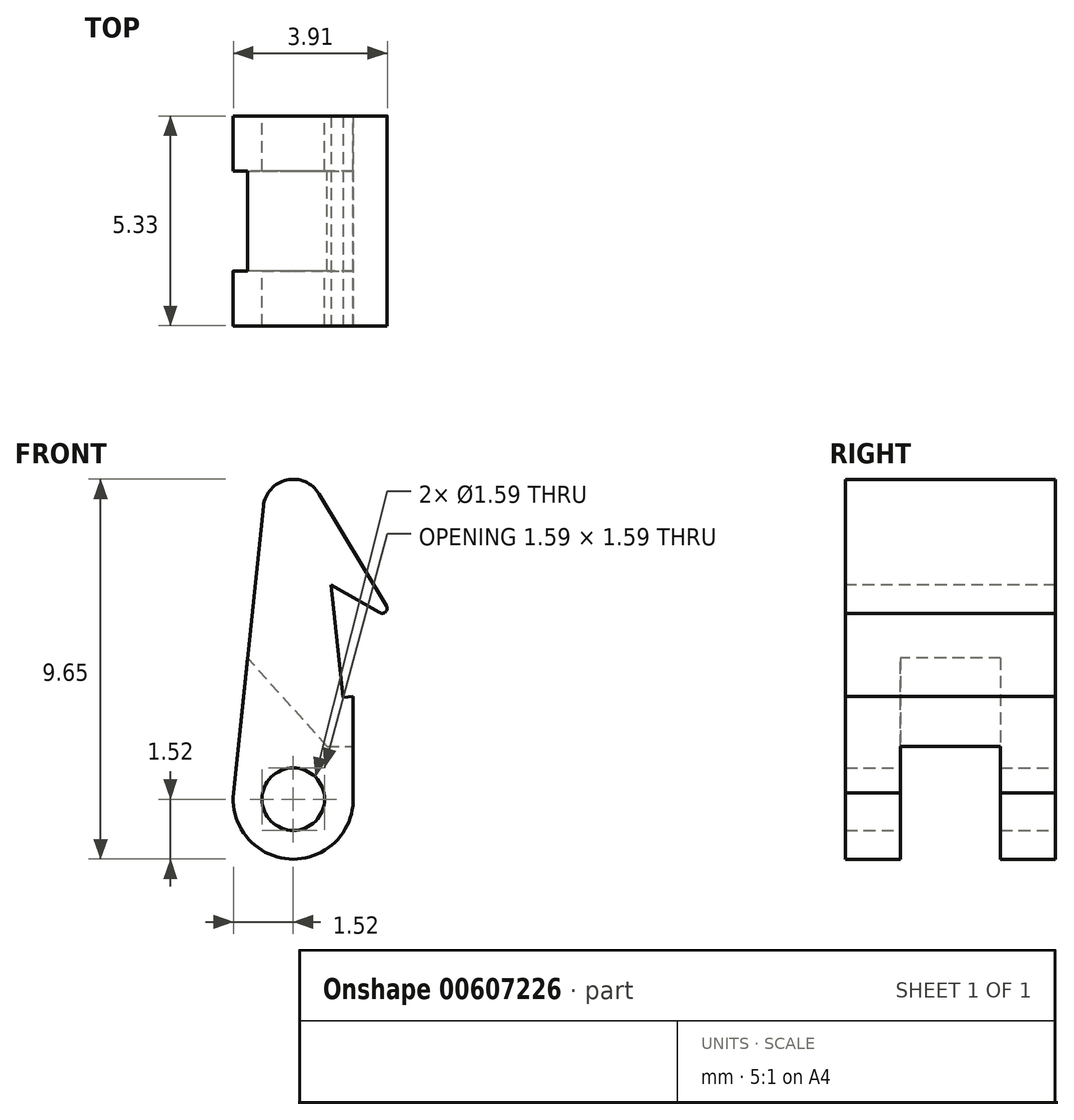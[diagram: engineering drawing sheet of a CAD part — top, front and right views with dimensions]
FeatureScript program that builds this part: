
annotation { "Feature Type Name" : "Feature", "Feature Type Description" : "" }
export const myFeature = defineFeature(function(context is Context, id is Id, definition is map)
    precondition{}
    {
        {
            var Q0;
            Q0=qCreatedBy(makeId("Front.planeOp"),FACE);
            var sketch = newSketch(context, id + "F0", { "sketchPlane" : qUnion([Q0])});
            skArc(sketch, "E0", {"start": v(1.52, 0.16) * mm, "mid": v(0, -1.52) * mm, "end": v(-1.52, 0.16) * mm});
            skLineSegment(sketch, "E1", {"start": v(-1.52, 0.16) * mm, "end": v(-0.76, 7.44) * mm});
            skArc(sketch, "E2", {"start": v(-0.76, 7.44) * mm, "mid": v(0, 8.13) * mm, "end": v(0.76, 7.44) * mm});
            skLineSegment(sketch, "E3", {"start": v(0.76, 7.44) * mm, "end": v(1.52, 0.16) * mm});
            skCircle(sketch, "E4", {"center": v(0, 0) * mm, "radius": 0.8 * mm});
            skSolve(sketch);
        }
        {
            var Q0;
            Q0 = qSketchRegion(id + "F0", true);
            extrude(context, id + "F1", {"entities" : qUnion([Q0]), "depth" : 5.33 * mm, "offsetDistance" : 25.4 * mm});
        }
        {
            var Q0;
            Q0=makeQuery(id+"F1.opExtrude","CAP_FACE",FACE,{"disambiguationData":[OSD([sQuery(id+"F0.wireOp",EDGE,"E0"),sQuery(id+"F0.wireOp",EDGE,"E1"),sQuery(id+"F0.wireOp",EDGE,"E2"),sQuery(id+"F0.wireOp",EDGE,"E3")])],"isStart":false});
            var sketch = newSketch(context, id + "F2", { "sketchPlane" : qUnion([Q0])});
            skLineSegment(sketch, "E5", {"start": v(0.65, 7.76) * mm, "end": v(2.62, 4.5) * mm});
            skLineSegment(sketch, "E6", {"start": v(2.62, 4.5) * mm, "end": v(0.97, 5.44) * mm});
            skLineSegment(sketch, "E7.0", {"start": v(0.76, 7.44) * mm, "end": v(1.52, 0.16) * mm});
            skArc(sketch, "E8.0", {"start": v(-0.76, 7.44) * mm, "mid": v(0, 8.13) * mm, "end": v(0.76, 7.44) * mm});
            skLineSegment(sketch, "E9", {"start": v(1.52, 0.16) * mm, "end": v(1.52, 2.61) * mm});
            skLineSegment(sketch, "E10", {"start": v(1.52, 2.61) * mm, "end": v(1.26, 2.59) * mm});
            skSolve(sketch);
        }
        {
            var Q0;
            Q0 = qSketchRegion(id + "F2", true);
            var Q1;
            {var subQ0=sQuery(id+"F2.wireOp",EDGE,"E5");Q1=makeQuery(id+"F2.imprint","IMPRINT",FACE,{"disambiguationData":[TD([[makeQuery(id+"F2.imprint","IMPRINT",EDGE,{"derivedFrom":subQ0}),-1.0]])]});}
            var Q2;
            Q2=makeQuery(id+"F1.opExtrude","CAP_FACE",FACE,{"disambiguationData":[OSD([sQuery(id+"F0.wireOp",EDGE,"E0"),sQuery(id+"F0.wireOp",EDGE,"E1"),sQuery(id+"F0.wireOp",EDGE,"E2"),sQuery(id+"F0.wireOp",EDGE,"E3"),sQuery(id+"F0.wireOp",EDGE,"E4")])],"isStart":true});
            extrude(context, id + "F3", {"entities" : qUnion([Q0, Q1]), "operationType" : NewBodyOperationType.ADD, "endBound" : BoundingType.UP_TO_SURFACE, "oppositeDirection" : true, "depth" : 25.4 * mm, "endBoundEntityFace" : qUnion([Q2]), "offsetDistance" : 25.4 * mm});
        }
        {
            var Q0;
            Q0=makeQuery(id+"F3.opExtrude","SWEPT_EDGE",EDGE,{"disambiguationData":[OSD([sQuery(id+"F2.wireOp",EDGE,"E5"),sQuery(id+"F2.wireOp",EDGE,"E6")])]});
            var Q1;
            Q1=makeQuery(id+"F3.opExtrude","SWEPT_EDGE",EDGE,{"disambiguationData":[OSD([sQuery(id+"F2.wireOp",EDGE,"E6"),sQuery(id+"F2.wireOp",EDGE,"E7.0")])]});
            fillet(context, id + "F4", {"entities" : qUnion([Q0, Q1]), "radius" : 0.13 * mm, "tangentPropagation" : true, "allowEdgeOverflow" : false});
        }
        {
            var Q0;
            Q0=makeQuery(id+"F3.opExtrude","SWEPT_FACE",FACE,{"disambiguationData":[OSD([sQuery(id+"F2.wireOp",EDGE,"E9")])]});
            var sketch = newSketch(context, id + "F5", { "sketchPlane" : qUnion([Q0])});
            skLineSegment(sketch, "E11.0.0", {"start": v(0, 0.16) * mm, "end": v(0, -1.52) * mm, "construction": true});
            skLineSegment(sketch, "E11.0.2", {"start": v(-5.33, 0.16) * mm, "end": v(-5.33, -1.52) * mm, "construction": true});
            skLineSegment(sketch, "E12.bottom", {"start": v(-3.94, -1.52) * mm, "end": v(-1.4, -1.52) * mm});
            skLineSegment(sketch, "E12.top", {"start": v(-3.94, 1.34) * mm, "end": v(-1.4, 1.34) * mm});
            skLineSegment(sketch, "E12.left", {"start": v(-3.94, -1.52) * mm, "end": v(-3.94, 1.34) * mm});
            skLineSegment(sketch, "E12.right", {"start": v(-1.4, -1.52) * mm, "end": v(-1.4, 1.34) * mm});
            skLineSegment(sketch, "E13", {"start": v(-5.33, -1.52) * mm, "end": v(-3.94, -1.52) * mm, "construction": true});
            skLineSegment(sketch, "E14", {"start": v(0, -1.52) * mm, "end": v(-1.4, -1.52) * mm, "construction": true});
            skSolve(sketch);
        }
        {
            var Q0;
            Q0 = qSketchRegion(id + "F5", true);
            extrude(context, id + "F6", {"entities" : qUnion([Q0]), "operationType" : NewBodyOperationType.REMOVE, "endBound" : BoundingType.THROUGH_ALL, "oppositeDirection" : true, "depth" : 25.4 * mm, "offsetDistance" : 25.4 * mm, "hasSecondDirection" : true, "secondDirectionBound" : SecondDirectionBoundingType.THROUGH_ALL, "secondDirectionOppositeDirection" : false, "secondDirectionDepth" : 25.4 * mm});
        }
        {
            var Q0;
            Q0=makeQuery(id+"F6.boolean.opBoolean","INTERSECT",EDGE,{"derivedFrom":[makeQuery(id+"F1.opExtrude","SWEPT_FACE",FACE,{"disambiguationData":[OSD([sQuery(id+"F0.wireOp",EDGE,"E1")])]}),makeQuery(id+"F6.opExtrude","SWEPT_FACE",FACE,{"disambiguationData":[OSD([sQuery(id+"F5.wireOp",EDGE,"E12.top")])]})]});
            chamfer(context, id + "F7", {"entities" : qUnion([Q0]), "width" : 2.03 * mm, "tangentPropagation" : true});
        }
    });
